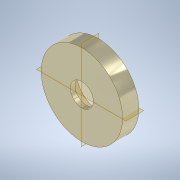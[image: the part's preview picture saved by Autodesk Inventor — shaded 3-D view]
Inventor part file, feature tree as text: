
AUTODESK INVENTOR PART (.ipt)
format: ipt  version: 2022 (Build 260153000, 153)  size: 105,472 bytes
history: native  units: mm
features: sketch x1, extrude x1, hole x1
ambient origin geometry x8: Origin, YZ Plane, XZ Plane, XY Plane, X Axis, Y Axis, Z Axis, Center Point
bodies: Solid1 (feature_tree)
feature tree (3):
  sketch  "Sketch1"  dims[d0=15.875mm d1=3.175mm d2=0.0mm d3=4.496mm d4=8.60806mm d5=8.433mm d6=2.0mm d7=14.3117mm d8=15.664mm d9=0.0mm]
  extrude  "Extrusion1"  Depth=3.175mm TaperAngle=0.0deg
  hole  "Hole1"  [1 undecoded]
note: 1 required parameter value undecoded (feature->parameter linkage not recoverable at this tier; creation-order binding heuristic only, values carry confidence <= 0.55)
